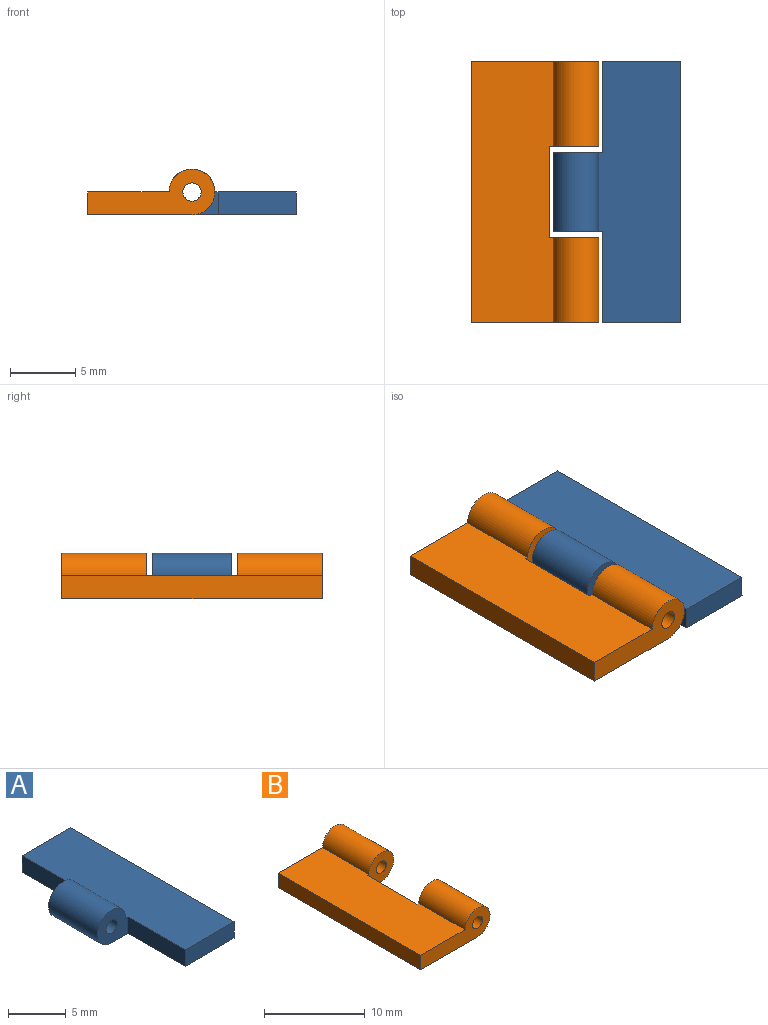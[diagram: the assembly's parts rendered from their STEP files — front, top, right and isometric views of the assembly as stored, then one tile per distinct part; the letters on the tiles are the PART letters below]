
ASSEMBLY  parts=2 mates=1
PART A: 11 faces, bbox 9.8x20x3.5 mm
  f0: plane 20x8mm, normal (0,0,-1), area 132mm2, adj f1,f3,f4,f5,f6,f7,f8,f9
  f1: cylinder r=1.75mm len=6mm, axis (0,1,0), area 49.5mm2, adj f0,f2,f6,f8
  f2: plane 20x6.25mm, normal (0,0,1), area 121.5mm2, adj f1,f3,f4,f5,f6,f7,f8,f9
  f3: plane 6x1.75mm, normal (0,-1,0), area 10.5mm2, adj f0,f2,f5,f9
  f4: plane 6x1.75mm, normal (0,1,0), area 10.5mm2, adj f0,f2,f5,f7
  f5: plane 20x1.75mm, normal (1,0,0), area 35mm2, adj f0,f2,f3,f4
  f6: plane 3.75x3.5mm, normal (0,1,0), area 9.2mm2, adj f0,f1,f2,f7,f10
  f7: plane 7x1.75mm, normal (-1,0,0), area 12.3mm2, adj f0,f2,f4,f6
  f8: plane 3.75x3.5mm, normal (0,-1,0), area 9.2mm2, adj f0,f1,f2,f9,f10
  f9: plane 7x1.75mm, normal (-1,0,0), area 12.3mm2, adj f0,f2,f3,f8
  f10: cylinder r=0.7mm len=6mm, axis (0,1,0), area 26.4mm2, adj f6,f8
PART B: 12 faces, bbox 9.8x20x3.5 mm
  f0: cylinder r=1.75mm len=6.5mm, axis (0,1,0), area 53.6mm2, adj f2,f4,f8,f10
  f1: cylinder r=0.7mm len=6.5mm, axis (0,1,0), area 28.6mm2, adj f8,f10
  f2: plane 20x8mm, normal (0,0,-1), area 146mm2, adj f0,f3,f6,f7,f8,f9,f10,f11
  f3: cylinder r=1.75mm len=6.5mm, axis (0,1,0), area 53.6mm2, adj f2,f4,f7,f9
  f4: plane 20x6.25mm, normal (0,0,1), area 123.3mm2, adj f0,f3,f6,f7,f8,f9,f10,f11
  f5: cylinder r=0.7mm len=6.5mm, axis (0,1,0), area 28.6mm2, adj f7,f9
  f6: plane 20x1.75mm, normal (-1,0,0), area 35mm2, adj f2,f4,f7,f8
  f7: plane 9.75x3.5mm, normal (0,-1,0), area 19.7mm2, adj f2,f3,f4,f5,f6
  f8: plane 9.75x3.5mm, normal (0,1,0), area 19.7mm2, adj f0,f1,f2,f4,f6
  f9: plane 3.75x3.5mm, normal (0,1,0), area 9.2mm2, adj f2,f3,f4,f5,f11
  f10: plane 3.75x3.5mm, normal (0,-1,0), area 9.2mm2, adj f0,f1,f2,f4,f11
  f11: plane 7x1.75mm, normal (1,0,0), area 12.3mm2, adj f2,f4,f9,f10
PLACE A t=(6.57,7.85,7.43)mm
PLACE B t=(6.57,7.85,7.43)mm
MATE revolute A.f10 <-> B.f1  axis (0,1,0) through (6.57,0.85,7.43)mm
